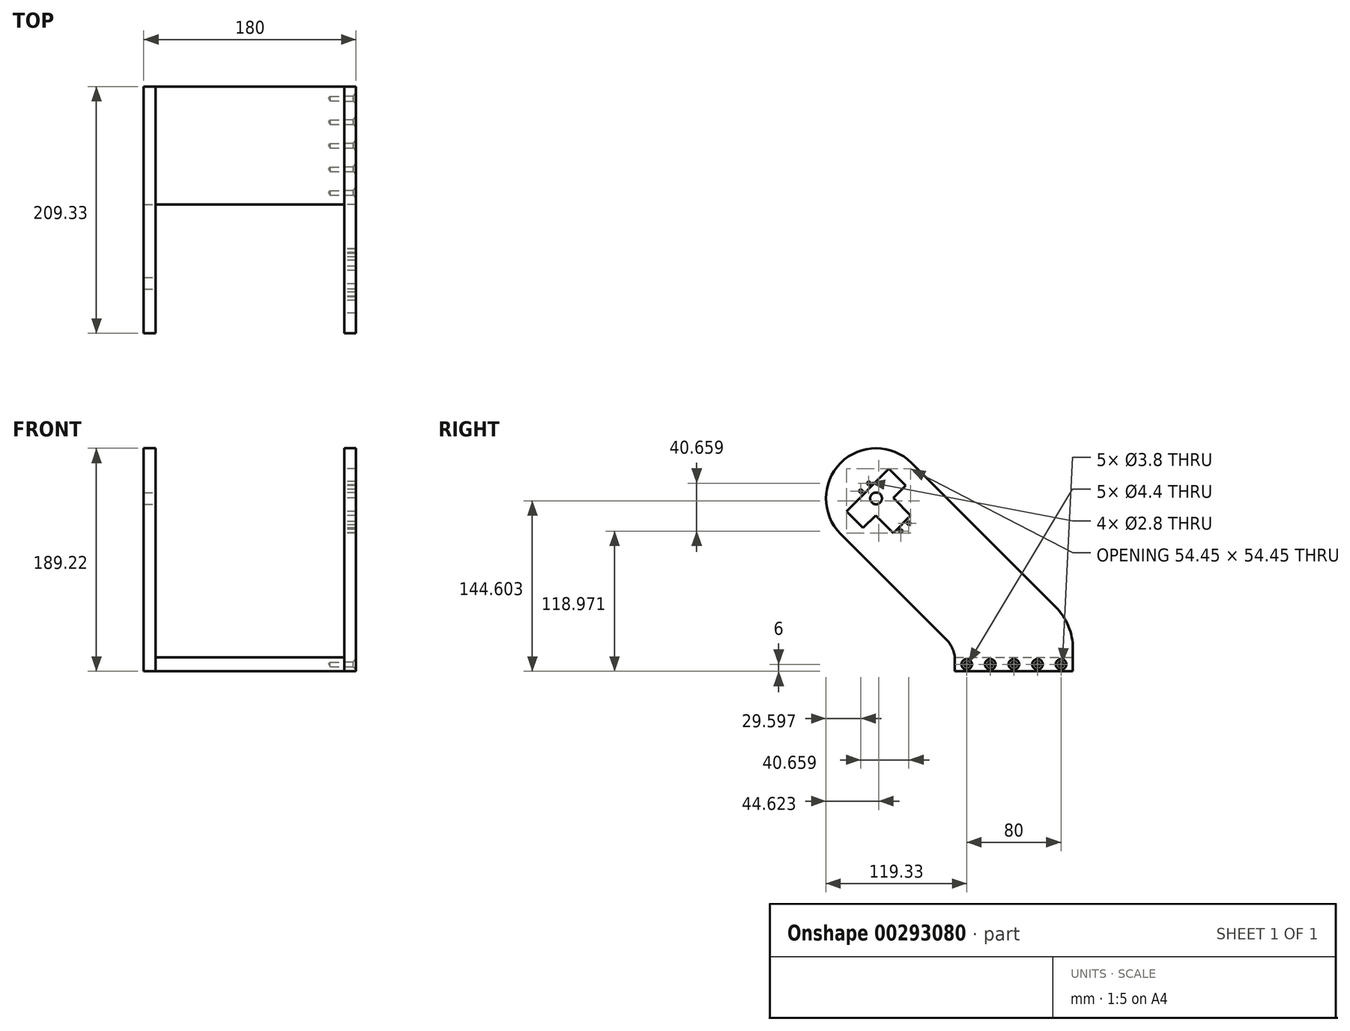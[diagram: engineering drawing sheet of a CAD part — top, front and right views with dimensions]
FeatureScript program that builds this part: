
annotation { "Feature Type Name" : "Feature", "Feature Type Description" : "" }
export const myFeature = defineFeature(function(context is Context, id is Id, definition is map)
    precondition{}
    {
        {
            var Q0;
            Q0=qCreatedBy(makeId("Right.planeOp"),FACE);
            var sketch = newSketch(context, id + "F0", { "sketchPlane" : qUnion([Q0])});
            skLineSegment(sketch, "E0", {"start": v(-40, 0) * mm, "end": v(-140, 0) * mm});
            skLineSegment(sketch, "E1", {"start": v(-147.32, 27.11) * mm, "end": v(-236.88, 116.67) * mm});
            skLineSegment(sketch, "E2", {"start": v(-236.88, 116.67) * mm, "end": v(-176.78, 176.78) * mm, "construction": true});
            skLineSegment(sketch, "E3", {"start": v(-176.78, 176.78) * mm, "end": v(-54.64, 54.64) * mm});
            skArc(sketch, "E4", {"start": v(-176.78, 176.78) * mm, "mid": v(-236.88, 176.78) * mm, "end": v(-236.88, 116.67) * mm});
            skCircle(sketch, "E5", {"center": v(-206.83, 146.72) * mm, "radius": 5 * mm});
            skLineSegment(sketch, "E6", {"start": v(-213.9, 153.8) * mm, "end": v(-184.9, 124.8) * mm, "construction": true});
            skLineSegment(sketch, "E7", {"start": v(-177.48, 132.23) * mm, "end": v(-192.33, 147.08) * mm});
            skLineSegment(sketch, "E8", {"start": v(-207.18, 132.23) * mm, "end": v(-192.33, 117.38) * mm});
            skLineSegment(sketch, "E9", {"start": v(-192.33, 117.38) * mm, "end": v(-177.48, 132.23) * mm});
            skPoint(sketch, "E10", {"position": v(-184.9, 124.8) * mm});
            skLineSegment(sketch, "E11", {"start": v(-140, 9.44) * mm, "end": v(-140, 0) * mm});
            skPoint(sketch, "E12.visualSharp", {"position": v(-140, 19.8) * mm});
            skArc(sketch, "E12.filletArc", {"start": v(-140, 9.44) * mm, "mid": v(-141.9, 19) * mm, "end": v(-147.32, 27.11) * mm});
            skLineSegment(sketch, "E13", {"start": v(-40, 19.29) * mm, "end": v(-40, 0) * mm});
            skPoint(sketch, "E14.orphan", {"position": v(0, 0) * mm});
            skPoint(sketch, "E15.visualSharp", {"position": v(-40, 40) * mm});
            skArc(sketch, "E15.filletArc", {"start": v(-40, 19.29) * mm, "mid": v(-43.8, 38.42) * mm, "end": v(-54.64, 54.64) * mm});
            skLineSegment(sketch, "E16", {"start": v(-195.87, 171.83) * mm, "end": v(-181.73, 157.68) * mm});
            skLineSegment(sketch, "E17", {"start": v(-181.73, 157.68) * mm, "end": v(-192.33, 147.08) * mm});
            skLineSegment(sketch, "E18", {"start": v(-195.87, 171.83) * mm, "end": v(-231.93, 135.76) * mm});
            skLineSegment(sketch, "E19", {"start": v(-231.93, 135.76) * mm, "end": v(-217.79, 121.62) * mm});
            skLineSegment(sketch, "E20", {"start": v(-217.79, 121.62) * mm, "end": v(-207.18, 132.23) * mm});
            skPoint(sketch, "E21", {"position": v(-188.8, 164.76) * mm});
            skLineSegment(sketch, "E22", {"start": v(-184.9, 124.8) * mm, "end": v(-182.43, 122.33) * mm, "construction": true});
            skLineSegment(sketch, "E23", {"start": v(-213.9, 153.8) * mm, "end": v(-216.37, 156.27) * mm, "construction": true});
            skLineSegment(sketch, "E24", {"start": v(-213.02, 159.63) * mm, "end": v(-219.73, 152.91) * mm, "construction": true});
            skLineSegment(sketch, "E25", {"start": v(-185.8, 118.97) * mm, "end": v(-179.07, 125.69) * mm, "construction": true});
            skCircle(sketch, "E26", {"center": v(-219.73, 152.91) * mm, "radius": 1.4 * mm});
            skCircle(sketch, "E27", {"center": v(-213.02, 159.63) * mm, "radius": 1.4 * mm});
            skCircle(sketch, "E28", {"center": v(-185.8, 118.97) * mm, "radius": 1.4 * mm});
            skCircle(sketch, "E29", {"center": v(-179.07, 125.69) * mm, "radius": 1.4 * mm});
            skCircle(sketch, "E30", {"center": v(-206.83, 146.72) * mm, "radius": 11 * mm});
            skSolve(sketch);
        }
        {
            var Q0;
            Q0=makeQuery(id+"F0.imprint","IMPRINT",FACE,{"disambiguationData":[TD([[makeQuery(id+"F0.imprint","IMPRINT",EDGE,{"derivedFrom":sQuery(id+"F0.wireOp",EDGE,"E0")}),-1.0]])]});
            var Q1;
            {var subQ0=sQuery(id+"F0.wireOp",EDGE,"E30");var subQ1=sQuery(id+"F0.wireOp",EDGE,"E18");var subQ2=makeQuery(id+"F0.imprint","INTERSECT",VERTEX,{"disambiguationData":[OD(0.0)],"derivedFrom":[subQ1,subQ0]});Q1=makeQuery(id+"F0.imprint","IMPRINT",FACE,{"disambiguationData":[TD([[makeQuery(id+"F0.imprint","IMPRINT",EDGE,{"disambiguationData":[TD([[subQ2,-1.0]])],"derivedFrom":subQ1}),-1.0]])]});}
            extrude(context, id + "F1", {"entities" : qUnion([Q0, Q1]), "depth" : 90 * mm, "hasSecondDirection" : true, "secondDirectionOppositeDirection" : false, "secondDirectionDepth" : 80 * mm});
        }
        {
            var Q0;
            Q0=makeQuery(id+"F0.imprint","IMPRINT",FACE,{"disambiguationData":[TD([[makeQuery(id+"F0.imprint","IMPRINT",EDGE,{"derivedFrom":sQuery(id+"F0.wireOp",EDGE,"E0")}),-1.0]])]});
            var Q1;
            Q1=makeQuery(id+"F0.imprint","IMPRINT",FACE,{"disambiguationData":[TD([[makeQuery(id+"F0.imprint","IMPRINT",EDGE,{"derivedFrom":sQuery(id+"F0.wireOp",EDGE,"E28")}),1.0]])]});
            var Q2;
            Q2=makeQuery(id+"F0.imprint","IMPRINT",FACE,{"disambiguationData":[TD([[makeQuery(id+"F0.imprint","IMPRINT",EDGE,{"derivedFrom":sQuery(id+"F0.wireOp",EDGE,"E29")}),1.0]])]});
            var Q3;
            Q3=makeQuery(id+"F0.imprint","IMPRINT",FACE,{"disambiguationData":[TD([[makeQuery(id+"F0.imprint","IMPRINT",EDGE,{"derivedFrom":sQuery(id+"F0.wireOp",EDGE,"E26")}),1.0]])]});
            var Q4;
            Q4=makeQuery(id+"F0.imprint","IMPRINT",FACE,{"disambiguationData":[TD([[makeQuery(id+"F0.imprint","IMPRINT",EDGE,{"derivedFrom":sQuery(id+"F0.wireOp",EDGE,"E27")}),1.0]])]});
            var Q5;
            Q5=makeQuery(id+"F0.imprint","IMPRINT",FACE,{"disambiguationData":[TD([[makeQuery(id+"F0.imprint","IMPRINT",EDGE,{"derivedFrom":sQuery(id+"F0.wireOp",EDGE,"E5")}),-1.0]])]});
            var Q6;
            {var subQ0=sQuery(id+"F0.wireOp",EDGE,"E30");var subQ1=sQuery(id+"F0.wireOp",EDGE,"E18");var subQ2=makeQuery(id+"F0.imprint","INTERSECT",VERTEX,{"disambiguationData":[OD(0.0)],"derivedFrom":[subQ1,subQ0]});Q6=makeQuery(id+"F0.imprint","IMPRINT",FACE,{"disambiguationData":[TD([[makeQuery(id+"F0.imprint","IMPRINT",EDGE,{"disambiguationData":[TD([[subQ2,-1.0]])],"derivedFrom":subQ1}),-1.0]])]});}
            var Q7;
            Q7=makeQuery(id+"F0.imprint","IMPRINT",FACE,{"disambiguationData":[TD([[makeQuery(id+"F0.imprint","IMPRINT",EDGE,{"derivedFrom":sQuery(id+"F0.wireOp",EDGE,"E7")}),1.0]])]});
            extrude(context, id + "F2", {"entities" : qUnion([Q0, Q1, Q2, Q3, Q4, Q5, Q6, Q7]), "oppositeDirection" : true, "depth" : 90 * mm, "hasSecondDirection" : true, "secondDirectionOppositeDirection" : true, "secondDirectionDepth" : 80 * mm});
        }
        {
            var Q0;
            Q0=qCreatedBy(makeId("Top.planeOp"),FACE);
            var sketch = newSketch(context, id + "F3", { "sketchPlane" : qUnion([Q0])});
            skLineSegment(sketch, "E31.0", {"start": v(0, -40) * mm, "end": v(0, -140) * mm, "construction": true});
            skLineSegment(sketch, "E32.bottom", {"start": v(-80, -140) * mm, "end": v(80, -140) * mm});
            skLineSegment(sketch, "E32.top", {"start": v(-80, -40) * mm, "end": v(80, -40) * mm});
            skLineSegment(sketch, "E32.left", {"start": v(-80, -140) * mm, "end": v(-80, -40) * mm});
            skLineSegment(sketch, "E32.right", {"start": v(80, -140) * mm, "end": v(80, -40) * mm});
            skCircle(sketch, "E33", {"center": v(0, -90) * mm, "radius": 50 * mm});
            skSolve(sketch);
        }
        {
            var Q0;
            {var subQ0=sQuery(id+"F3.wireOp",EDGE,"E33");var subQ1=makeQuery(id+"F3.imprint","INTERSECT",VERTEX,{"derivedFrom":[sQuery(id+"F3.wireOp",EDGE,"E32.top"),subQ0]});Q0=makeQuery(id+"F3.imprint","IMPRINT",FACE,{"disambiguationData":[TD([[makeQuery(id+"F3.imprint","IMPRINT",EDGE,{"disambiguationData":[TD([[subQ1,1.0]])],"derivedFrom":subQ0}),1.0]])]});}
            var Q1;
            {var subQ0=sQuery(id+"F3.wireOp",EDGE,"E32.left");var subQ1=sQuery(id+"F3.wireOp",EDGE,"E32.bottom");var subQ2=makeQuery(id+"F3.imprint","INTERSECT",VERTEX,{"derivedFrom":[subQ1,subQ0]});Q1=makeQuery(id+"F3.imprint","IMPRINT",FACE,{"disambiguationData":[TD([[makeQuery(id+"F3.imprint","IMPRINT",EDGE,{"disambiguationData":[TD([[subQ2,-1.0]])],"derivedFrom":subQ1}),1.0]])]});}
            var Q2;
            {var subQ0=sQuery(id+"F3.wireOp",EDGE,"E32.left");var subQ1=sQuery(id+"F3.wireOp",EDGE,"E32.top");var subQ2=makeQuery(id+"F3.imprint","INTERSECT",VERTEX,{"derivedFrom":[subQ1,subQ0]});Q2=makeQuery(id+"F3.imprint","IMPRINT",FACE,{"disambiguationData":[TD([[makeQuery(id+"F3.imprint","IMPRINT",EDGE,{"disambiguationData":[TD([[subQ2,-1.0]])],"derivedFrom":subQ1}),-1.0]])]});}
            var Q3;
            {var subQ0=sQuery(id+"F3.wireOp",EDGE,"E32.right");var subQ1=sQuery(id+"F3.wireOp",EDGE,"E32.top");var subQ2=makeQuery(id+"F3.imprint","INTERSECT",VERTEX,{"derivedFrom":[subQ1,subQ0]});Q3=makeQuery(id+"F3.imprint","IMPRINT",FACE,{"disambiguationData":[TD([[makeQuery(id+"F3.imprint","IMPRINT",EDGE,{"disambiguationData":[TD([[subQ2,1.0]])],"derivedFrom":subQ1}),-1.0]])]});}
            var Q4;
            {var subQ0=sQuery(id+"F3.wireOp",EDGE,"E32.right");var subQ1=sQuery(id+"F3.wireOp",EDGE,"E32.bottom");var subQ2=makeQuery(id+"F3.imprint","INTERSECT",VERTEX,{"derivedFrom":[subQ1,subQ0]});Q4=makeQuery(id+"F3.imprint","IMPRINT",FACE,{"disambiguationData":[TD([[makeQuery(id+"F3.imprint","IMPRINT",EDGE,{"disambiguationData":[TD([[subQ2,1.0]])],"derivedFrom":subQ1}),1.0]])]});}
            extrude(context, id + "F4", {"entities" : qUnion([Q0, Q1, Q2, Q3, Q4]), "depth" : 12 * mm});
        }
        {
            var Q0;
            Q0=makeQuery(id+"F1.opExtrude","CAP_FACE",FACE,{"disambiguationData":[OSD([sQuery(id+"F0.wireOp",EDGE,"E0"),sQuery(id+"F0.wireOp",EDGE,"E1"),sQuery(id+"F0.wireOp",EDGE,"E3"),sQuery(id+"F0.wireOp",EDGE,"E4"),sQuery(id+"F0.wireOp",EDGE,"E7"),sQuery(id+"F0.wireOp",EDGE,"WQ5BBzSV-Ko4y-NPwg-SSiC-7ToHBexHt3mH"),sQuery(id+"F0.wireOp",EDGE,"E8"),sQuery(id+"F0.wireOp",EDGE,"E9"),sQuery(id+"F0.wireOp",EDGE,"E11"),sQuery(id+"F0.wireOp",EDGE,"E12.filletArc"),sQuery(id+"F0.wireOp",EDGE,"E13"),sQuery(id+"F0.wireOp",EDGE,"E15.filletArc")])],"isStart":false});
            var sketch = newSketch(context, id + "F5", { "sketchPlane" : qUnion([Q0])});
            skLineSegment(sketch, "E34", {"start": v(-140, 6) * mm, "end": v(-40, 6) * mm, "construction": true});
            skLineSegment(sketch, "E35", {"start": v(-90, 6) * mm, "end": v(-90, 0) * mm, "construction": true});
            skPoint(sketch, "E36", {"position": v(-90, 6) * mm});
            skPoint(sketch, "E37", {"position": v(-110, 6) * mm});
            skPoint(sketch, "E38", {"position": v(-130, 6) * mm});
            skPoint(sketch, "E39", {"position": v(-70, 6) * mm});
            skPoint(sketch, "E40", {"position": v(-50, 6) * mm});
            skSolve(sketch);
        }
        {
            var Q0;
            Q0=sQuery(id+"F5.wireOp",VERTEX,"E38");
            var Q1;
            Q1=sQuery(id+"F5.wireOp",VERTEX,"E37");
            var Q2;
            Q2=sQuery(id+"F5.wireOp",VERTEX,"E39");
            var Q3;
            Q3=sQuery(id+"F5.wireOp",VERTEX,"E40");
            var Q4;
            Q4=sQuery(id+"F5.wireOp",VERTEX,"E36");
            var Q5;
            Q5=makeQuery(id+"F1.opExtrude","SWEPT_BODY",BODY,{"disambiguationData":[OSD([sQuery(id+"F0.wireOp",EDGE,"E0"),sQuery(id+"F0.wireOp",EDGE,"E1"),sQuery(id+"F0.wireOp",EDGE,"E3"),sQuery(id+"F0.wireOp",EDGE,"E4"),sQuery(id+"F0.wireOp",EDGE,"E7"),sQuery(id+"F0.wireOp",EDGE,"WQ5BBzSV-Ko4y-NPwg-SSiC-7ToHBexHt3mH"),sQuery(id+"F0.wireOp",EDGE,"E8"),sQuery(id+"F0.wireOp",EDGE,"E9"),sQuery(id+"F0.wireOp",EDGE,"E11"),sQuery(id+"F0.wireOp",EDGE,"E12.filletArc"),sQuery(id+"F0.wireOp",EDGE,"E13"),sQuery(id+"F0.wireOp",EDGE,"E15.filletArc")])]});
            var Q6;
            Q6=makeQuery(id+"F2.opExtrude","SWEPT_BODY",BODY,{"disambiguationData":[OSD([sQuery(id+"F0.wireOp",EDGE,"E0"),sQuery(id+"F0.wireOp",EDGE,"E1"),sQuery(id+"F0.wireOp",EDGE,"E3"),sQuery(id+"F0.wireOp",EDGE,"E4"),sQuery(id+"F0.wireOp",EDGE,"E5"),sQuery(id+"F0.wireOp",EDGE,"E11"),sQuery(id+"F0.wireOp",EDGE,"E12.filletArc"),sQuery(id+"F0.wireOp",EDGE,"E13"),sQuery(id+"F0.wireOp",EDGE,"E15.filletArc")])]});
            hole(context, id + "F6", {"style" : HoleStyle.C_SINK, "endStyle" : HoleEndStyle.BLIND, "standardTappedOrClearance" : lookupTablePath({ "standard" : "ISO", "fit" : "Normal", "size" : "M4", "type" : "Clearance" }), "standardBlindInLast" : lookupTablePath({ "fit" : "Standard", "standard" : "ISO", "size" : "M4", "type" : "Clearance" }), "holeDiameter" : 4.4 * mm, "cSinkDiameter" : 8.96 * mm, "cSinkAngle" : 90 * degree, "holeDepth" : 10 * mm, "tappedDepth" : 12 * mm, "tapClearance" : 3, "locations" : qUnion([Q0, Q1, Q2, Q3, Q4]), "scope" : qUnion([Q5, Q6])});
        }
        {
            var Q0;
            Q0=sQuery(id+"F5.wireOp",VERTEX,"E38");
            var Q1;
            Q1=sQuery(id+"F5.wireOp",VERTEX,"E37");
            var Q2;
            Q2=sQuery(id+"F5.wireOp",VERTEX,"E36");
            var Q3;
            Q3=sQuery(id+"F5.wireOp",VERTEX,"E39");
            var Q4;
            Q4=sQuery(id+"F5.wireOp",VERTEX,"E40");
            var Q5;
            Q5=makeQuery(id+"F4.opExtrude","SWEPT_BODY",BODY,{"disambiguationData":[OSD([sQuery(id+"F3.wireOp",EDGE,"E32.bottom"),sQuery(id+"F3.wireOp",EDGE,"E32.top"),sQuery(id+"F3.wireOp",EDGE,"E32.left"),sQuery(id+"F3.wireOp",EDGE,"E32.right")])]});
            hole(context, id + "F7", {"style" : HoleStyle.SIMPLE, "endStyle" : HoleEndStyle.BLIND, "standardTappedOrClearance" : lookupTablePath({ "standard" : "ISO", "size" : "3.8", "type" : "Drilled" }), "standardBlindInLast" : lookupTablePath({ "standard" : "ISO", "size" : "3.8", "type" : "Drilled" }), "holeDiameter" : 3.8 * mm, "holeDepth" : 12 * mm, "tappedDepth" : 12 * mm, "tapClearance" : 3, "locations" : qUnion([Q0, Q1, Q2, Q3, Q4]), "scope" : qUnion([Q5])});
        }
    });
